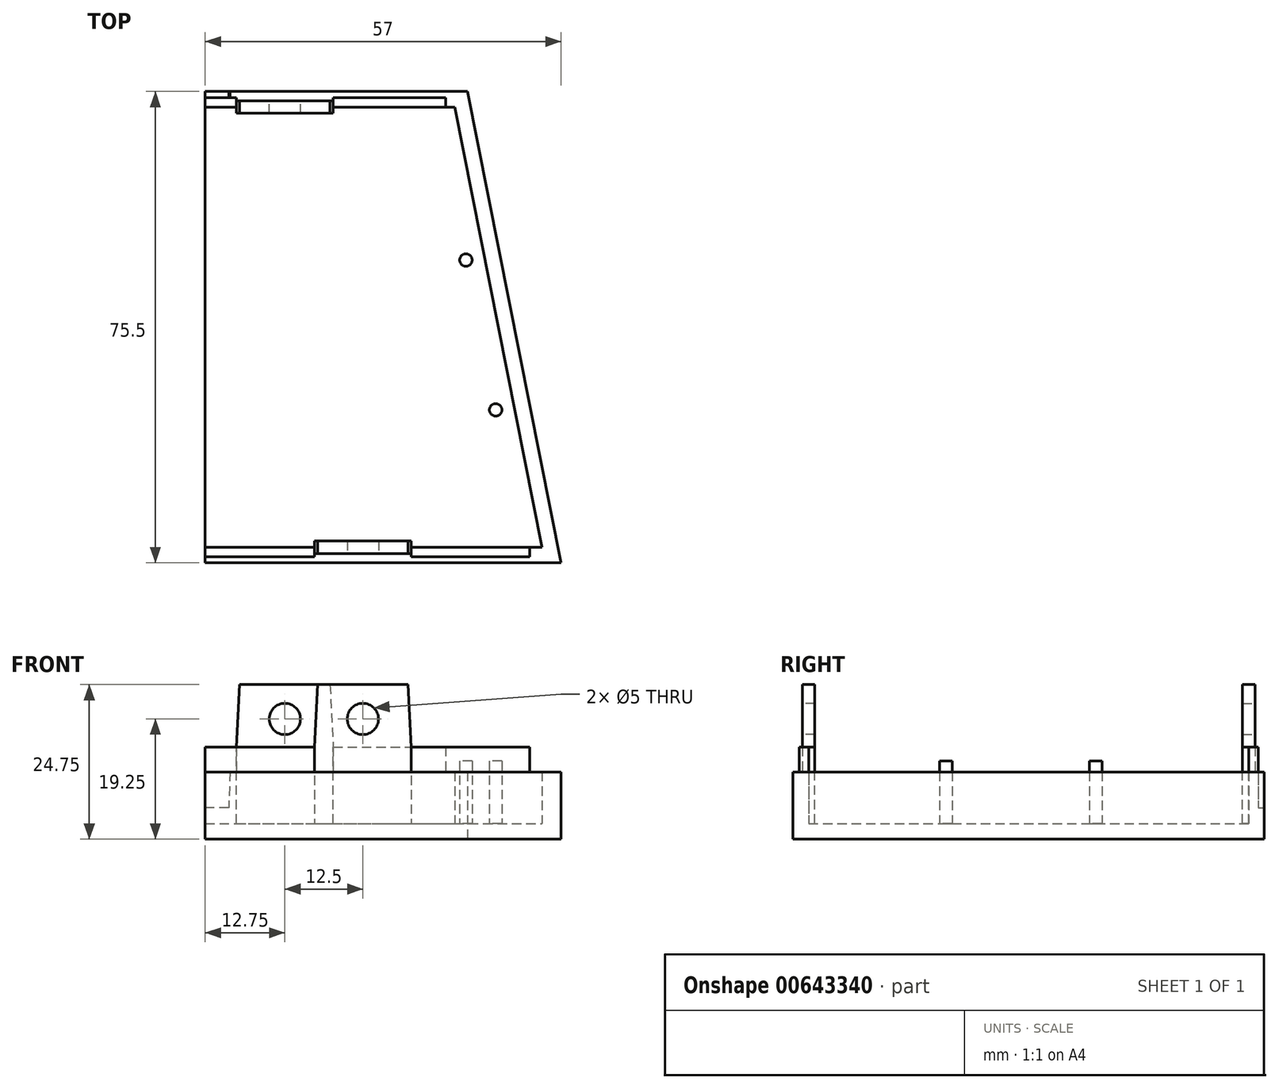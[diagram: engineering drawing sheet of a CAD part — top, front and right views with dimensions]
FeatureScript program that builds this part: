
annotation { "Feature Type Name" : "Feature", "Feature Type Description" : "" }
export const myFeature = defineFeature(function(context is Context, id is Id, definition is map)
    precondition{}
    {
        {
            var Q0;
            Q0=qCreatedBy(makeId("Top.planeOp"),FACE);
            var sketch = newSketch(context, id + "F0", { "sketchPlane" : qUnion([Q0])});
            skLineSegment(sketch, "E0.bottom", {"start": v(21, -37.75) * mm, "end": v(-21, -37.75) * mm});
            skLineSegment(sketch, "E0.top", {"start": v(21, 37.75) * mm, "end": v(-21, 37.75) * mm});
            skLineSegment(sketch, "E0.left", {"start": v(21, -37.75) * mm, "end": v(21, 37.75) * mm});
            skLineSegment(sketch, "E0.right", {"start": v(-21, -37.75) * mm, "end": v(-21, 37.75) * mm});
            skPoint(sketch, "E0.middle", {"position": v(0, 0) * mm});
            skLineSegment(sketch, "E1", {"start": v(21, -37.75) * mm, "end": v(36, -37.75) * mm});
            skLineSegment(sketch, "E2", {"start": v(36, -37.75) * mm, "end": v(21, 37.75) * mm});
            skSolve(sketch);
        }
        {
            var Q0;
            Q0=makeQuery(id+"F0.imprint","IMPRINT",FACE,{"disambiguationData":[TD([[makeQuery(id+"F0.imprint","IMPRINT",EDGE,{"derivedFrom":sQuery(id+"F0.wireOp",EDGE,"E0.bottom")}),-1.0]])]});
            var Q1;
            Q1=makeQuery(id+"F0.imprint","IMPRINT",FACE,{"disambiguationData":[TD([[makeQuery(id+"F0.imprint","IMPRINT",EDGE,{"derivedFrom":sQuery(id+"F0.wireOp",EDGE,"E0.left")}),-1.0]])]});
            extrude(context, id + "F1", {"entities" : qUnion([Q0, Q1]), "depth" : 2.5 * mm, "offsetDistance" : 25 * mm});
        }
        {
            var Q0;
            Q0=makeQuery(id+"F1.opExtrude","CAP_FACE",FACE,{"disambiguationData":[OSD([sQuery(id+"F0.wireOp",EDGE,"E0.bottom"),sQuery(id+"F0.wireOp",EDGE,"E0.top"),sQuery(id+"F0.wireOp",EDGE,"E0.right"),sQuery(id+"F0.wireOp",EDGE,"E1"),sQuery(id+"F0.wireOp",EDGE,"E2")])],"isStart":false});
            var sketch = newSketch(context, id + "F2", { "sketchPlane" : qUnion([Q0])});
            skLineSegment(sketch, "E3", {"start": v(-21, 37.75) * mm, "end": v(-21, 35.25) * mm});
            skLineSegment(sketch, "E4", {"start": v(-21, 35.25) * mm, "end": v(21.5, 35.25) * mm});
            skLineSegment(sketch, "E5", {"start": v(-21, -35.25) * mm, "end": v(35.5, -35.25) * mm});
            skLineSegment(sketch, "E6", {"start": v(18.45, 37.75) * mm, "end": v(33.45, -37.75) * mm});
            skSolve(sketch);
        }
        {
            var Q0;
            {var subQ0=sQuery(id+"F2.wireOp",EDGE,"E4");var subQ1=makeQuery(id+"F1.opExtrude","CAP_EDGE",EDGE,{"disambiguationData":[OSD([sQuery(id+"F0.wireOp",EDGE,"E2")])],"isStart":false});var subQ2=makeQuery(id+"F2.imprint","INTERSECT",VERTEX,{"derivedFrom":[subQ1,subQ0]});Q0=makeQuery(id+"F2.imprint","IMPRINT",FACE,{"disambiguationData":[TD([[makeQuery(id+"F2.imprint","IMPRINT",EDGE,{"disambiguationData":[TD([[subQ2,1.0]])],"derivedFrom":subQ0}),-1.0]])]});}
            var Q1;
            {var subQ0=sQuery(id+"F2.wireOp",EDGE,"E3");Q1=makeQuery(id+"F2.imprint","IMPRINT",FACE,{"disambiguationData":[TD([[makeQuery(id+"F2.imprint","IMPRINT",EDGE,{"derivedFrom":subQ0}),-1.0]])]});}
            var Q2;
            {var subQ0=sQuery(id+"F2.wireOp",EDGE,"E5");var subQ1=makeQuery(id+"F1.opExtrude","CAP_EDGE",EDGE,{"disambiguationData":[OSD([sQuery(id+"F0.wireOp",EDGE,"E0.right")])],"isStart":false});var subQ2=makeQuery(id+"F2.imprint","INTERSECT",VERTEX,{"derivedFrom":[subQ1,subQ0]});Q2=makeQuery(id+"F2.imprint","IMPRINT",FACE,{"disambiguationData":[TD([[makeQuery(id+"F2.imprint","IMPRINT",EDGE,{"disambiguationData":[TD([[subQ2,-1.0]])],"derivedFrom":subQ0}),-1.0]])]});}
            var Q3;
            {var subQ0=sQuery(id+"F2.wireOp",EDGE,"E4");var subQ1=makeQuery(id+"F1.opExtrude","CAP_EDGE",EDGE,{"disambiguationData":[OSD([sQuery(id+"F0.wireOp",EDGE,"E2")])],"isStart":false});var subQ2=makeQuery(id+"F2.imprint","INTERSECT",VERTEX,{"derivedFrom":[subQ1,subQ0]});Q3=makeQuery(id+"F2.imprint","IMPRINT",FACE,{"disambiguationData":[TD([[makeQuery(id+"F2.imprint","IMPRINT",EDGE,{"disambiguationData":[TD([[subQ2,1.0]])],"derivedFrom":subQ0}),1.0]])]});}
            var Q4;
            {var subQ0=sQuery(id+"F2.wireOp",EDGE,"E5");var subQ1=makeQuery(id+"F1.opExtrude","CAP_EDGE",EDGE,{"disambiguationData":[OSD([sQuery(id+"F0.wireOp",EDGE,"E2")])],"isStart":false});var subQ2=makeQuery(id+"F2.imprint","INTERSECT",VERTEX,{"derivedFrom":[subQ1,subQ0]});Q4=makeQuery(id+"F2.imprint","IMPRINT",FACE,{"disambiguationData":[TD([[makeQuery(id+"F2.imprint","IMPRINT",EDGE,{"disambiguationData":[TD([[subQ2,1.0]])],"derivedFrom":subQ0}),-1.0]])]});}
            extrude(context, id + "F3", {"entities" : qUnion([Q0, Q1, Q2, Q3, Q4]), "operationType" : NewBodyOperationType.ADD, "depth" : 2.5 * mm, "offsetDistance" : 25 * mm});
        }
        {
            var Q0;
            Q0=makeQuery(id+"F3.opExtrude","CAP_FACE",FACE,{"disambiguationData":[OSD([sQuery(id+"F0.wireOp",EDGE,"E0.bottom"),sQuery(id+"F0.wireOp",EDGE,"E0.top"),sQuery(id+"F0.wireOp",EDGE,"E0.right"),sQuery(id+"F0.wireOp",EDGE,"E1"),sQuery(id+"F0.wireOp",EDGE,"E2"),sQuery(id+"F2.wireOp",EDGE,"E3"),sQuery(id+"F2.wireOp",EDGE,"E4"),sQuery(id+"F2.wireOp",EDGE,"E5"),sQuery(id+"F2.wireOp",EDGE,"E6")])],"isStart":false});
            var sketch = newSketch(context, id + "F4", { "sketchPlane" : qUnion([Q0])});
            skSolve(sketch);
        }
        {
            var Q0;
            {var subQ1=sQuery(id+"F4.wireOp",EDGE,"8ttH36ro-W37B-LJvB-VMmp-QlwjvhTyqbqM");Q0=makeQuery(id+"F4.imprint","IMPRINT",FACE,{"disambiguationData":[TD([[makeQuery(id+"F4.imprint","IMPRINT",EDGE,{"derivedFrom":subQ1}),1.0]])]});}
            var Q1;
            Q1=makeQuery(id+"F4.imprint","IMPRINT",FACE,{"disambiguationData":[TD([[makeQuery(id+"F4.imprint","IMPRINT",EDGE,{"derivedFrom":makeQuery(id+"F3.opExtrude","CAP_EDGE",EDGE,{"disambiguationData":[OSD([sQuery(id+"F2.wireOp",EDGE,"E3")])],"isStart":false})}),-1.0]])]});
            extrude(context, id + "F5", {"entities" : qUnion([Q0, Q1]), "operationType" : NewBodyOperationType.ADD, "depth" : 5.75 * mm, "offsetDistance" : 25 * mm});
        }
        {
            var Q0;
            Q0=makeQuery(id+"F5.opExtrude","CAP_FACE",FACE,{"disambiguationData":[OSD([sQuery(id+"F0.wireOp",EDGE,"E0.bottom"),sQuery(id+"F0.wireOp",EDGE,"E0.top"),sQuery(id+"F0.wireOp",EDGE,"E0.right"),sQuery(id+"F0.wireOp",EDGE,"E1"),sQuery(id+"F0.wireOp",EDGE,"E2"),sQuery(id+"F2.wireOp",EDGE,"E4"),sQuery(id+"F2.wireOp",EDGE,"E5"),sQuery(id+"F2.wireOp",EDGE,"E6"),sQuery(id+"F4.wireOp",EDGE,"8ttH36ro-W37B-LJvB-VMmp-QlwjvhTyqbqM")])],"isStart":false});
            var sketch = newSketch(context, id + "F6", { "sketchPlane" : qUnion([Q0])});
            skSolve(sketch);
        }
        {
            var Q0;
            {var subQ0=sQuery(id+"F0.wireOp",EDGE,"E0.top");Q0=makeQuery(id+"F5.boolean.opBoolean","MERGE",FACE,{"derivedFrom":[makeQuery(id+"F3.boolean.opBoolean","MERGE",FACE,{"derivedFrom":[makeQuery(id+"F1.opExtrude","SWEPT_FACE",FACE,{"disambiguationData":[OSD([subQ0])]}),makeQuery(id+"F3.opExtrude","SWEPT_FACE",FACE,{"disambiguationData":[OSD([subQ0])]})]}),makeQuery(id+"F5.opExtrude","SWEPT_FACE",FACE,{"disambiguationData":[OSD([subQ0])]})]});}
            var sketch = newSketch(context, id + "F7", { "sketchPlane" : qUnion([Q0])});
            skLineSegment(sketch, "E7", {"start": v(21, 10.75) * mm, "end": v(17, 10.75) * mm});
            skLineSegment(sketch, "E8", {"start": v(17, 10.75) * mm, "end": v(17.25, 5) * mm});
            skLineSegment(sketch, "E9", {"start": v(17.25, 5) * mm, "end": v(21, 5) * mm});
            skSolve(sketch);
        }
        {
            var Q0;
            {var subQ0=sQuery(id+"F7.wireOp",EDGE,"E7");Q0=makeQuery(id+"F7.imprint","IMPRINT",FACE,{"disambiguationData":[TD([[makeQuery(id+"F7.imprint","IMPRINT",EDGE,{"derivedFrom":subQ0}),-1.0]])]});}
            extrude(context, id + "F8", {"entities" : qUnion([Q0]), "operationType" : NewBodyOperationType.REMOVE, "oppositeDirection" : true, "depth" : 1 * mm, "offsetDistance" : 25 * mm});
        }
        {
            var Q0;
            Q0=makeQuery(id+"F6.imprint","IMPRINT",FACE,{"disambiguationData":[TD([[makeQuery(id+"F6.imprint","IMPRINT",EDGE,{"derivedFrom":makeQuery(id+"F5.opExtrude","CAP_EDGE",EDGE,{"disambiguationData":[OSD([sQuery(id+"F2.wireOp",EDGE,"E3")])],"isStart":false})}),-1.0]])]});
            var sketch = newSketch(context, id + "F9", { "sketchPlane" : qUnion([Q0])});
            skLineSegment(sketch, "E10", {"start": v(-21, 35.25) * mm, "end": v(17.5, 35.25) * mm});
            skLineSegment(sketch, "E11", {"start": v(17.5, 35.25) * mm, "end": v(17.5, 36.75) * mm});
            skLineSegment(sketch, "E12", {"start": v(17.5, 36.75) * mm, "end": v(-21, 36.75) * mm});
            skLineSegment(sketch, "E13", {"start": v(-21, 36.75) * mm, "end": v(-21, 35.25) * mm});
            skLineSegment(sketch, "E14.bottom", {"start": v(31, -35.25) * mm, "end": v(-21, -35.25) * mm});
            skLineSegment(sketch, "E14.top", {"start": v(31, -36.75) * mm, "end": v(-21, -36.75) * mm});
            skLineSegment(sketch, "E14.left", {"start": v(31, -35.25) * mm, "end": v(31, -36.75) * mm});
            skLineSegment(sketch, "E14.right", {"start": v(-21, -35.25) * mm, "end": v(-21, -36.75) * mm});
            skPoint(sketch, "E14.middle", {"position": v(5, -36) * mm});
            skSolve(sketch);
        }
        {
            var Q0;
            Q0 = qSketchRegion(id + "F9", true);
            extrude(context, id + "F10", {"entities" : qUnion([Q0]), "operationType" : NewBodyOperationType.ADD, "depth" : 4 * mm, "offsetDistance" : 25 * mm});
        }
        {
            var Q0;
            Q0=makeQuery(id+"F10.opExtrude","SWEPT_FACE",FACE,{"disambiguationData":[OSD([sQuery(id+"F9.wireOp",EDGE,"E14.top")])]});
            var sketch = newSketch(context, id + "F11", { "sketchPlane" : qUnion([Q0])});
            skLineSegment(sketch, "E15.bottom", {"start": v(-3.5, 14.75) * mm, "end": v(12, 14.75) * mm});
            skLineSegment(sketch, "E15.top", {"start": v(-3.5, 10.75) * mm, "end": v(12, 10.75) * mm});
            skLineSegment(sketch, "E15.left", {"start": v(-3.5, 14.75) * mm, "end": v(-3.5, 10.75) * mm});
            skLineSegment(sketch, "E15.right", {"start": v(12, 14.75) * mm, "end": v(12, 10.75) * mm});
            skSolve(sketch);
        }
        {
            var Q0;
            Q0=makeQuery(id+"F11.imprint","IMPRINT",FACE,{"disambiguationData":[TD([[makeQuery(id+"F11.imprint","IMPRINT",EDGE,{"derivedFrom":sQuery(id+"F11.wireOp",EDGE,"E15.bottom")}),1.0]])]});
            extrude(context, id + "F12", {"entities" : qUnion([Q0]), "operationType" : NewBodyOperationType.REMOVE, "oppositeDirection" : true, "depth" : .5 * mm, "offsetDistance" : 25 * mm});
        }
        {
            var Q0;
            Q0=makeQuery(id+"F10.boolean.opBoolean","MERGE",FACE,{"derivedFrom":[makeQuery(id+"F8.boolean.opBoolean","COPY",FACE,{"derivedFrom":makeQuery(id+"F8.opExtrude","CAP_FACE",FACE,{"disambiguationData":[OSD([sQuery(id+"F0.wireOp",EDGE,"E0.top"),sQuery(id+"F0.wireOp",EDGE,"E0.right"),sQuery(id+"F2.wireOp",EDGE,"E3"),sQuery(id+"F7.wireOp",EDGE,"E7"),sQuery(id+"F7.wireOp",EDGE,"E8"),sQuery(id+"F7.wireOp",EDGE,"E9")])],"isStart":false})}),makeQuery(id+"F10.opExtrude","SWEPT_FACE",FACE,{"disambiguationData":[OSD([sQuery(id+"F9.wireOp",EDGE,"E12")])]})]});
            var sketch = newSketch(context, id + "F13", { "sketchPlane" : qUnion([Q0])});
            skLineSegment(sketch, "E16.bottom", {"start": v(16, 14.75) * mm, "end": v(0.5, 14.75) * mm});
            skLineSegment(sketch, "E16.top", {"start": v(16, 10.75) * mm, "end": v(0.5, 10.75) * mm});
            skLineSegment(sketch, "E16.left", {"start": v(16, 14.75) * mm, "end": v(16, 10.75) * mm});
            skLineSegment(sketch, "E16.right", {"start": v(0.5, 14.75) * mm, "end": v(0.5, 10.75) * mm});
            skSolve(sketch);
        }
        {
            var Q0;
            Q0=makeQuery(id+"F13.imprint","IMPRINT",FACE,{"disambiguationData":[TD([[makeQuery(id+"F13.imprint","IMPRINT",EDGE,{"derivedFrom":sQuery(id+"F13.wireOp",EDGE,"E16.bottom")}),-1.0]])]});
            extrude(context, id + "F14", {"entities" : qUnion([Q0]), "operationType" : NewBodyOperationType.REMOVE, "oppositeDirection" : true, "depth" : .5 * mm, "offsetDistance" : 25 * mm});
        }
        {
            var Q0;
            Q0=makeQuery(id+"F10.opExtrude","CAP_FACE",FACE,{"disambiguationData":[OSD([sQuery(id+"F9.wireOp",EDGE,"E14.bottom"),sQuery(id+"F9.wireOp",EDGE,"E14.top"),sQuery(id+"F9.wireOp",EDGE,"E14.left"),sQuery(id+"F9.wireOp",EDGE,"E14.right")])],"isStart":false});
            var sketch = newSketch(context, id + "F15", { "sketchPlane" : qUnion([Q0])});
            skLineSegment(sketch, "E17.bottom", {"start": v(-3.5, -36.25) * mm, "end": v(12, -36.25) * mm});
            skLineSegment(sketch, "E17.top", {"start": v(-3.5, -34.25) * mm, "end": v(12, -34.25) * mm});
            skLineSegment(sketch, "E17.left", {"start": v(-3.5, -36.25) * mm, "end": v(-3.5, -34.25) * mm});
            skLineSegment(sketch, "E17.right", {"start": v(12, -36.25) * mm, "end": v(12, -34.25) * mm});
            skLineSegment(sketch, "E18.bottom", {"start": v(-16, 36.25) * mm, "end": v(-0.5, 36.25) * mm});
            skLineSegment(sketch, "E18.top", {"start": v(-16, 34.25) * mm, "end": v(-0.5, 34.25) * mm});
            skLineSegment(sketch, "E18.left", {"start": v(-16, 36.25) * mm, "end": v(-16, 34.25) * mm});
            skLineSegment(sketch, "E18.right", {"start": v(-0.5, 36.25) * mm, "end": v(-0.5, 34.25) * mm});
            skSolve(sketch);
        }
        {
            var Q0;
            {var subQ0=sQuery(id+"F15.wireOp",EDGE,"E17.bottom");Q0=makeQuery(id+"F15.imprint","IMPRINT",FACE,{"disambiguationData":[TD([[makeQuery(id+"F15.imprint","IMPRINT",EDGE,{"derivedFrom":subQ0}),-1.0]])]});}
            var Q1;
            {var subQ0=sQuery(id+"F15.wireOp",EDGE,"E17.top");Q1=makeQuery(id+"F15.imprint","IMPRINT",FACE,{"disambiguationData":[TD([[makeQuery(id+"F15.imprint","IMPRINT",EDGE,{"derivedFrom":subQ0}),-1.0]])]});}
            var Q2;
            Q2=makeQuery(id+"F15.imprint","IMPRINT",FACE,{"disambiguationData":[TD([[makeQuery(id+"F15.imprint","IMPRINT",EDGE,{"derivedFrom":sQuery(id+"F15.wireOp",EDGE,"E18.bottom")}),-1.0]])]});
            extrude(context, id + "F16", {"entities" : qUnion([Q0, Q1, Q2]), "operationType" : NewBodyOperationType.ADD, "oppositeDirection" : true, "depth" : 14.5 * mm, "offsetDistance" : 25 * mm, "hasSecondDirection" : true, "secondDirectionOppositeDirection" : false, "secondDirectionDepth" : 10 * mm});
        }
        {
            var Q0;
            Q0=makeQuery(id+"F16.opExtrude","CAP_EDGE",EDGE,{"disambiguationData":[OSD([sQuery(id+"F15.wireOp",EDGE,"E18.right")])],"isStart":true});
            var Q1;
            Q1=makeQuery(id+"F16.opExtrude","CAP_EDGE",EDGE,{"disambiguationData":[OSD([sQuery(id+"F15.wireOp",EDGE,"E18.left")])],"isStart":true});
            chamfer(context, id + "F17", {"entities" : qUnion([Q0, Q1]), "chamferType" : ChamferType.TWO_OFFSETS, "width1" : 10 * mm, "oppositeDirection" : false, "width2" : .5 * mm, "tangentPropagation" : true});
        }
        {
            var Q0;
            Q0=makeQuery(id+"F16.opExtrude","CAP_EDGE",EDGE,{"disambiguationData":[OSD([sQuery(id+"F15.wireOp",EDGE,"E17.right")])],"isStart":true});
            var Q1;
            Q1=makeQuery(id+"F16.opExtrude","CAP_EDGE",EDGE,{"disambiguationData":[OSD([sQuery(id+"F15.wireOp",EDGE,"E17.left")])],"isStart":true});
            chamfer(context, id + "F18", {"entities" : qUnion([Q0, Q1]), "chamferType" : ChamferType.TWO_OFFSETS, "width1" : .5 * mm, "oppositeDirection" : false, "width2" : 10 * mm, "tangentPropagation" : true});
        }
        {
            var Q0;
            Q0=makeQuery(id+"F16.boolean.opBoolean","MERGE",FACE,{"derivedFrom":[makeQuery(id+"F14.boolean.opBoolean","COPY",FACE,{"derivedFrom":makeQuery(id+"F14.opExtrude","CAP_FACE",FACE,{"disambiguationData":[OSD([sQuery(id+"F13.wireOp",EDGE,"E16.bottom"),sQuery(id+"F13.wireOp",EDGE,"E16.top"),sQuery(id+"F13.wireOp",EDGE,"E16.left"),sQuery(id+"F13.wireOp",EDGE,"E16.right")])],"isStart":false})}),makeQuery(id+"F16.opExtrude","SWEPT_FACE",FACE,{"disambiguationData":[OSD([sQuery(id+"F15.wireOp",EDGE,"E18.bottom")])]})]});
            var sketch = newSketch(context, id + "F19", { "sketchPlane" : qUnion([Q0])});
            skLineSegment(sketch, "E19", {"start": v(8.25, 24.75) * mm, "end": v(8.25, 21.75) * mm, "construction": true});
            skPoint(sketch, "E19.endSnap0", {"position": v(8.25, 24.75) * mm});
            skCircle(sketch, "E20", {"center": v(8.25, 19.25) * mm, "radius": 2.5 * mm});
            skSolve(sketch);
        }
        {
            var Q0;
            Q0=makeQuery(id+"F19.imprint","IMPRINT",FACE,{"disambiguationData":[TD([[makeQuery(id+"F19.imprint","IMPRINT",EDGE,{"derivedFrom":sQuery(id+"F19.wireOp",EDGE,"E20")}),1.0]])]});
            extrude(context, id + "F20", {"entities" : qUnion([Q0]), "operationType" : NewBodyOperationType.REMOVE, "endBound" : BoundingType.UP_TO_NEXT, "oppositeDirection" : true, "depth" : 25 * mm, "offsetDistance" : 25 * mm});
        }
        {
            var Q0;
            Q0=makeQuery(id+"F16.boolean.opBoolean","MERGE",FACE,{"derivedFrom":[makeQuery(id+"F12.boolean.opBoolean","COPY",FACE,{"derivedFrom":makeQuery(id+"F12.opExtrude","CAP_FACE",FACE,{"disambiguationData":[OSD([sQuery(id+"F11.wireOp",EDGE,"E15.bottom"),sQuery(id+"F11.wireOp",EDGE,"E15.top"),sQuery(id+"F11.wireOp",EDGE,"E15.left"),sQuery(id+"F11.wireOp",EDGE,"E15.right")])],"isStart":false})}),makeQuery(id+"F16.opExtrude","SWEPT_FACE",FACE,{"disambiguationData":[OSD([sQuery(id+"F15.wireOp",EDGE,"E17.bottom")])]})]});
            var sketch = newSketch(context, id + "F21", { "sketchPlane" : qUnion([Q0])});
            skLineSegment(sketch, "E21", {"start": v(4.25, 24.75) * mm, "end": v(4.25, 21.75) * mm, "construction": true});
            skCircle(sketch, "E22", {"center": v(4.25, 19.25) * mm, "radius": 2.5 * mm});
            skSolve(sketch);
        }
        {
            var Q0;
            Q0=makeQuery(id+"F21.imprint","IMPRINT",FACE,{"disambiguationData":[TD([[makeQuery(id+"F21.imprint","IMPRINT",EDGE,{"derivedFrom":sQuery(id+"F21.wireOp",EDGE,"E22")}),1.0]])]});
            extrude(context, id + "F22", {"entities" : qUnion([Q0]), "operationType" : NewBodyOperationType.REMOVE, "endBound" : BoundingType.UP_TO_NEXT, "oppositeDirection" : true, "depth" : 25 * mm, "offsetDistance" : 25 * mm});
        }
        {
            var Q0;
            Q0=makeQuery(id+"F1.opExtrude","CAP_FACE",FACE,{"disambiguationData":[OSD([sQuery(id+"F0.wireOp",EDGE,"E0.bottom"),sQuery(id+"F0.wireOp",EDGE,"E0.top"),sQuery(id+"F0.wireOp",EDGE,"E0.right"),sQuery(id+"F0.wireOp",EDGE,"E1"),sQuery(id+"F0.wireOp",EDGE,"E2")])],"isStart":false});
            var sketch = newSketch(context, id + "F23", { "sketchPlane" : qUnion([Q0])});
            skCircle(sketch, "E23", {"center": v(25.52, -13.25) * mm, "radius": 1 * mm});
            skCircle(sketch, "E24", {"center": v(20.76, 10.75) * mm, "radius": 1 * mm});
            skSolve(sketch);
        }
        {
            var Q0;
            Q0=makeQuery(id+"F23.imprint","IMPRINT",FACE,{"disambiguationData":[TD([[makeQuery(id+"F23.imprint","IMPRINT",EDGE,{"derivedFrom":sQuery(id+"F23.wireOp",EDGE,"E24")}),1.0]])]});
            var Q1;
            Q1=makeQuery(id+"F23.imprint","IMPRINT",FACE,{"disambiguationData":[TD([[makeQuery(id+"F23.imprint","IMPRINT",EDGE,{"derivedFrom":sQuery(id+"F23.wireOp",EDGE,"E23")}),1.0]])]});
            extrude(context, id + "F24", {"entities" : qUnion([Q0, Q1]), "operationType" : NewBodyOperationType.ADD, "depth" : 10 * mm, "offsetDistance" : 25 * mm});
        }
    });
